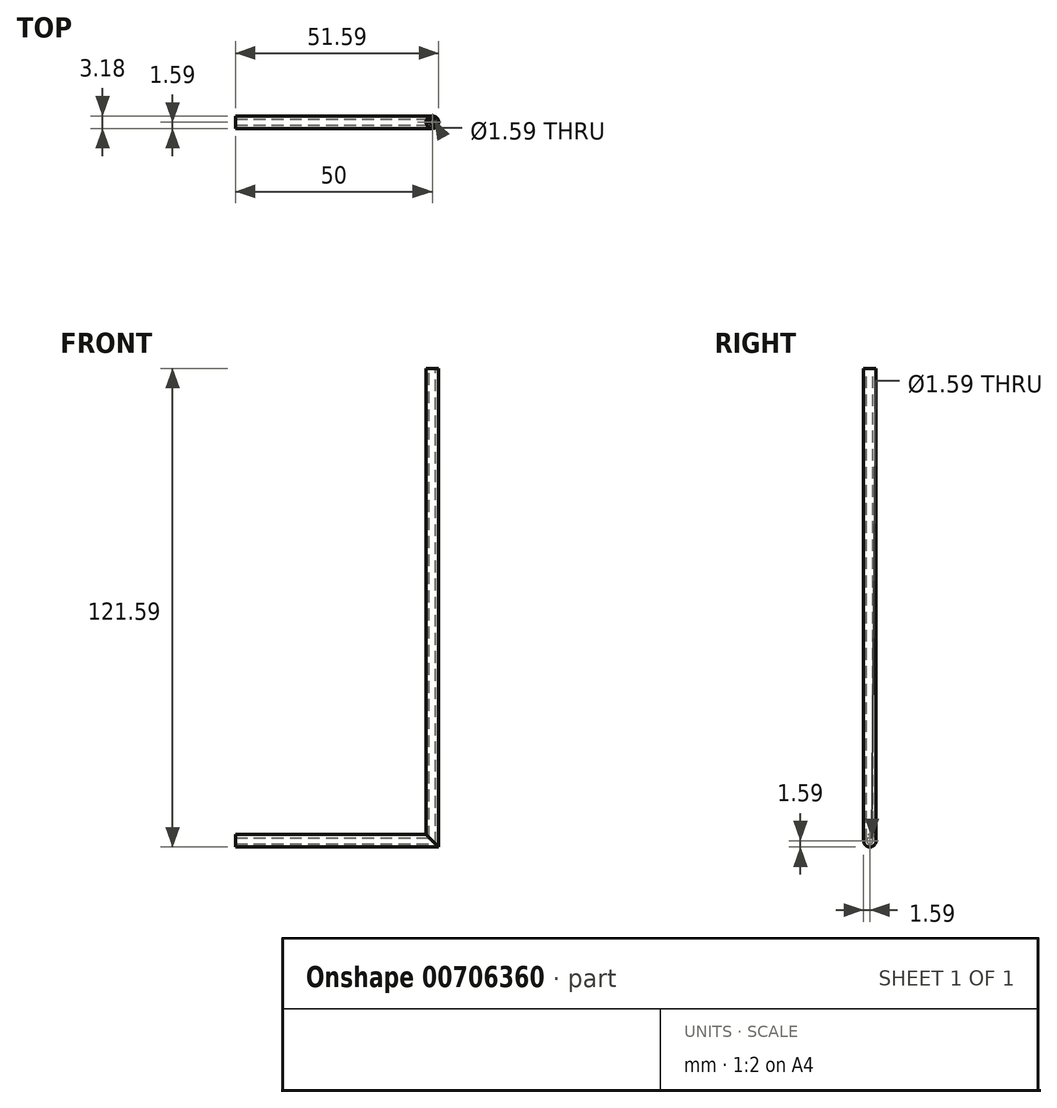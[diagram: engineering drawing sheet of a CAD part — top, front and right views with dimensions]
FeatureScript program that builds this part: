
annotation { "Feature Type Name" : "Feature", "Feature Type Description" : "" }
export const myFeature = defineFeature(function(context is Context, id is Id, definition is map)
    precondition{}
    {
        {
            var Q0;
            Q0=qCreatedBy(makeId("Right.planeOp"),FACE);
            var sketch = newSketch(context, id + "F0", { "sketchPlane" : qUnion([Q0])});
            skCircle(sketch, "E0", {"center": v(0, 0) * mm, "radius": 1.59 * mm});
            skSolve(sketch);
        }
        {
            var Q0;
            Q0=qCreatedBy(makeId("Right.planeOp"),FACE);
            var sketch = newSketch(context, id + "F1", { "sketchPlane" : qUnion([Q0])});
            skCircle(sketch, "E1", {"center": v(0, 0) * mm, "radius": 0.8 * mm});
            skSolve(sketch);
        }
        {
            var Q0;
            Q0=qCreatedBy(makeId("Front.planeOp"),FACE);
            var sketch = newSketch(context, id + "F2", { "sketchPlane" : qUnion([Q0])});
            skLineSegment(sketch, "E2", {"start": v(0, 0) * mm, "end": v(50, 0) * mm});
            skLineSegment(sketch, "E3", {"start": v(50, 0) * mm, "end": v(50, 120) * mm});
            skSolve(sketch);
        }
        {
            var Q0;
            Q0=makeQuery(id+"F0.imprint","IMPRINT",FACE,{"disambiguationData":[TD([[makeQuery(id+"F0.imprint","IMPRINT",EDGE,{"derivedFrom":sQuery(id+"F0.wireOp",EDGE,"E0")}),1.0]])]});
            var Q1;
            Q1 = qConstructionFilter(qBodyType(qCreatedBy(id + "F2" ,EDGE), BodyType.WIRE), ConstructionObject.NO);
            sweep(context, id + "F3", {"profiles" : qUnion([Q0]), "path" : qUnion([Q1])});
        }
        {
            var Q0;
            Q0=makeQuery(id+"F1.imprint","IMPRINT",FACE,{"disambiguationData":[TD([[makeQuery(id+"F1.imprint","IMPRINT",EDGE,{"derivedFrom":sQuery(id+"F1.wireOp",EDGE,"E1")}),1.0]])]});
            var Q1;
            Q1 = qConstructionFilter(qBodyType(qCreatedBy(id + "F2" ,EDGE), BodyType.WIRE), ConstructionObject.NO);
            sweep(context, id + "F4", {"operationType" : NewBodyOperationType.REMOVE, "profiles" : qUnion([Q0]), "path" : qUnion([Q1])});
        }
    });
